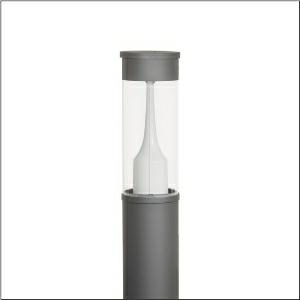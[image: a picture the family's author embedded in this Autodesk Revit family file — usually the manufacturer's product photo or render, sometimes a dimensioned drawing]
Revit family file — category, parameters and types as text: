
# Revit family: city-light_260_iq___st1_2a_5xa5295af14h_a960
name_source: partatom
category: Lighting Fixtures
units: mm (PartAtom-declared; Revit-internal decimal feet)

## family parameters
Cut with Voids When Loaded = No
Host = Face
Light Source = No
Part Type = Normal
Room Calculation Point = No
Round Connector Dimension = Use Diameter
Shared = No

## types (1)
- --- (1 x LED, 1540 lm, 12.9 W, 2200K)
    Apparent Load = 13 VA
    CIE Flux Codes = 22 61 93 96 100
    Color Rendering = 70
    Color Temperature = 2200K
    Default Elevation = 1800 mm
    Description = City-Light 260 iQ, light pillar, Module 540 iQ-SR, primary light control with 3 zone facetted reflector, of plastic, silver coated, highly specular, structured, primary optical cover: cover, of PMMA, transparent, partly coated, light distribution: ST1.2a, primary light characteristic: asymmetric, LED, High Power LED, rated luminous flux: 1.540lm, luminous efficacy: 119lm/W, light colour: 722, colour temperature: 2200K, control gear: iQ Street-Remote, control: pre-setting: logarithmic dimming characteristic, Street-Remote, Auto-Match, Temp-Guard, Lumen-Switch, Night-Set, Smart-Wire, Light-Fading, Desk-Remote (wireless, voltage-free reading and setting of iQ features in the workshop via application-optimized NFC function/RFID function), optimised constant luminous flux control (CLO 2.0), with terminal, 6-pole, max. 2.5mm², mains connection: 230..240V, AC, 50/60Hz, start of lifetime: 13W, end of service life: 13W, reduction: 6W, luminaire housing, cylindrical, of extruded aluminium section, coated, Siteco® metallic grey (DB 702S), length: 2.600mm, diameter: 200mm, Module 540 iQ-SR, traffic white (RAL 9016), equipment: standard, protection rating (complete): IP65, insulation class (complete): insulation class II (safety insulation), certification: CE, ENEC, VDE, packaging unit: 1 piece

Light Distribution: ST1.2a
    Height = 500 mm
    Lamp = 1 x LED
    Lamp Light Flux = 1540 lm
    Lamp Power = 12.9 W
    Lamp count = 1
    Length = 200 mm  [stored 0.656168 ft]
    Luminous efficacy = 119 lm/W
    Manufacturer = Siteco
    ModVariant = No
    Model = 5XA5295AF14H
    Mounting Place = Floor
    Mounting Type = Freestanding
    Number of Poles = 1
    OnlyDefault = Yes
    Power Factor = 1
    Product Name = City-Light 260 iQ | ST1.2a
    Product group = light pillar
    ProductGroupID = 1301
    Protection Class = Protection class II
    Protection Degree = IP 65
    RLX_Detail_Level = 1
    RLX_Emergency_Light_Flux = 0 lm
    RLX_Emergency_Type = 0
    RLX_Emergency_Type_DB = No
    RlxData = <blob elided: 54117 chars, md5=d388005f>
    Socket = socket
    Standby Power = 0 W
    System Light Flux = 1540 lm
    System Power = 13 W
    Type Comments = factory setting: luminous flux: 100 % | dim-lin: 254 | 516 mA
    Type Image = l_1006918.jpg
    URL = http://relux.com
    VarID = @adj_159260
    Voltage = 0 V
    Weight = 0.00 kg
    Width = 0 mm  [stored 0 ft]

note: [stored X ft] marks values corroborated as IEEE doubles in the binary element streams (Revit-internal decimal feet)

## geometry (parser evidence)
native form markers: Blend x4, Sweep x11
no freeform markers — native parametric forms only
